# Revit family: Rückflussverhinderer 4126
name_source: partatom
category: Rohrzubehör
revit_build: Autodesk Revit 2018 (Build: 20190510_1515(x64)
units: mm (PartAtom-declared; Revit-internal decimal feet)

## family parameters
Arbeitsebenenbasiert = Nein
Beim Laden mit Abzugskörper schneiden = Nein
Bemaßung runder Anschluss = Durchmesser verwenden
Gemeinsam genutzt = Nein
Immer vertikal = Ja
OmniClass-Nummer = 23.65.55.14
OmniClass-Titel = Valves for Liquid Services
Teiletyp = Unterbricht

## types (1)
- Rückflussverhinderer 4126
    Anwendungsgebiet = Zum Absperren von Trinkwasserleitungen, sowie Zirkulationssystemen in Gebäuden.
    Gehäuse = entzinkungsbeständiges Gussmessing CC770S
    Gelegentliche Temperaturanstiege = bis 95°C, nicht länger als eine Stunde
    Handrad = Kunststoff, grün
    Hersteller = HERZ Armaturen Ges.m.b.H.
    Hinweis = Gemäß Art 33 der REACH-Verordnung (EG Nr. 1907/2006) sind wir verpflichtet, darauf hinzuweisen, dass der Stoff Blei auf der SVHC-Liste geführt wird und dass alle aus Messing bestehenden Bauteile, die in unseren Erzeugnissen verarbeitet sind, mehr als 0,1 % (w/w) Blei (CAS: 7439-92-1 / EINECS: 231-100-4) enthalten.
Da Blei als Legierungsbestandteil fest gebunden ist, sind keine Expositionen zu erwarten und daher sind keine zusätzlichen Angaben zur sicheren Verwendung notwendig.
    Kegel = geschmiedetes Messing CW617N
    L03 = 15 mm  [stored 0.0492126 ft]
    Max. Betriebsdruck = 1600000.0 Pa
    Max. Betriebstemperatur = 80 °C
    Max. Differenzdruck auf geschlossenen Sitz = 1000000.0 Pa
    Medium = Trinkwasser
    R03 = 9.5 mm  [stored 0.031168 ft]
    R100 = 1 mm  [stored 0.00328084 ft]
    S03 = 60 mm  [stored 0.19685 ft]
    SCTWCODE = 04;00;02
    SCTWSEQ = FW;SBT_TYP_FW="109";2
    SC_NennweiteBerechnet = 0
    SW01 = 60.00°
    Spindel = geschmiedetes Messing CW617N
    URL = www.herz-armaturen.at
    W01 = 45.00°
    Öffnungsdruck des Rückflussverhinderer = gemäß DIN EN 13959

note: [stored X ft] marks values corroborated as IEEE doubles in the binary element streams (Revit-internal decimal feet)
